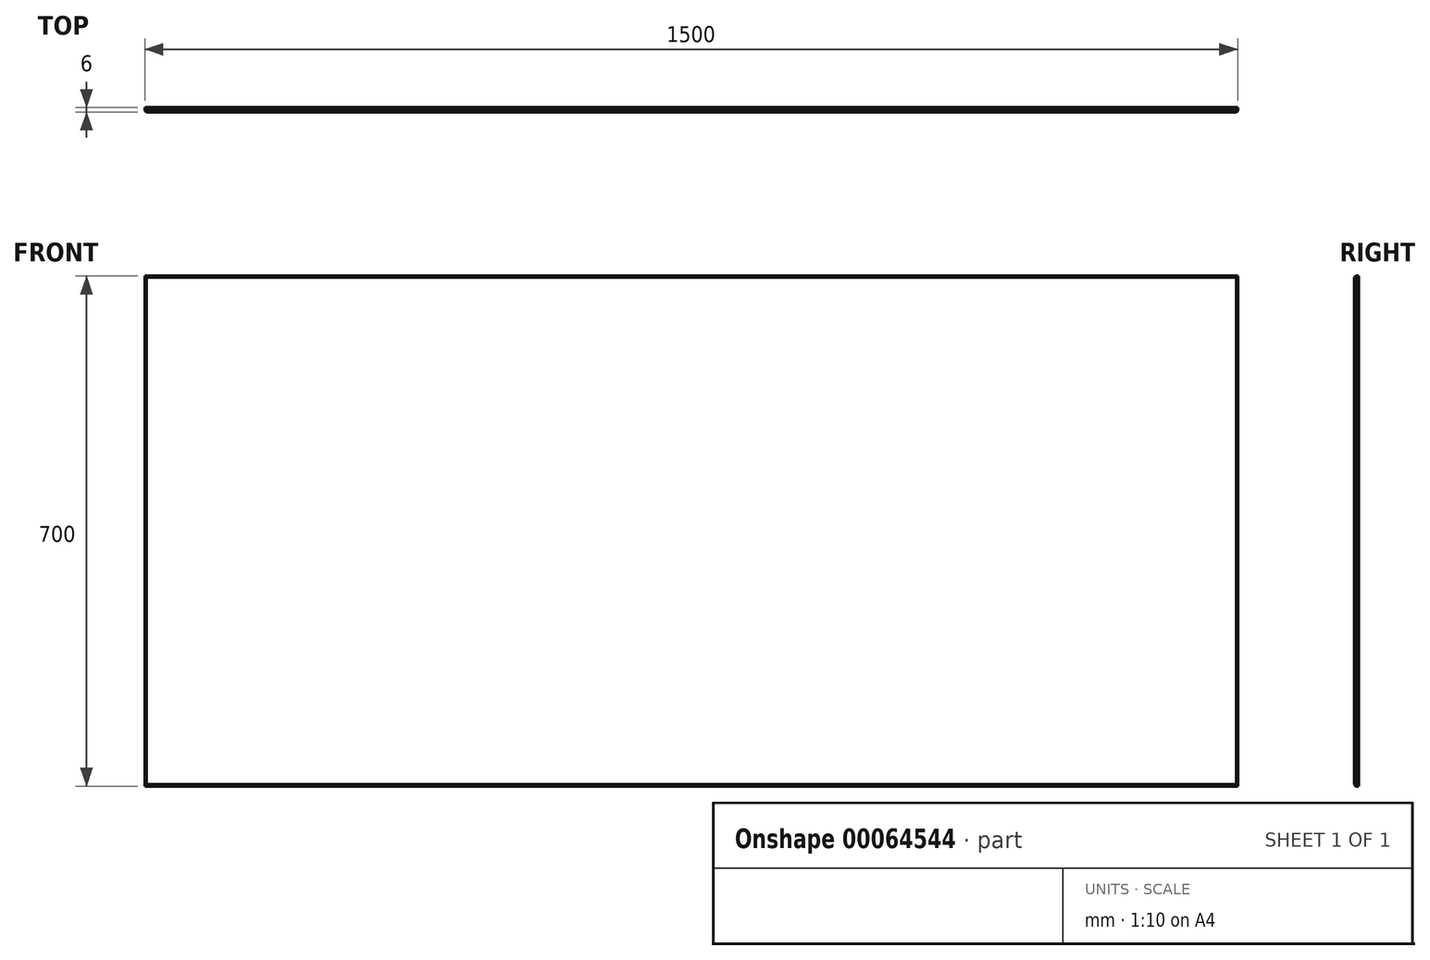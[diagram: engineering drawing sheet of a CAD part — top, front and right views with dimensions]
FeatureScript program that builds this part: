
annotation { "Feature Type Name" : "Feature", "Feature Type Description" : "" }
export const myFeature = defineFeature(function(context is Context, id is Id, definition is map)
    precondition{}
    {
        {
            var Q0;
            Q0=qCreatedBy(makeId("Front.planeOp"),FACE);
            var sketch = newSketch(context, id + "F0", { "sketchPlane" : qUnion([Q0])});
            skLineSegment(sketch, "E0.bottom", {"start": v(-741.76, 374.66) * mm, "end": v(758.24, 374.66) * mm});
            skLineSegment(sketch, "E0.top", {"start": v(-741.76, -325.34) * mm, "end": v(758.24, -325.34) * mm});
            skLineSegment(sketch, "E0.left", {"start": v(-741.76, 374.66) * mm, "end": v(-741.76, -325.34) * mm});
            skLineSegment(sketch, "E0.right", {"start": v(758.24, 374.66) * mm, "end": v(758.24, -325.34) * mm});
            skSolve(sketch);
        }
        {
            var Q0;
            Q0=makeQuery(id+"F0.imprint","IMPRINT",FACE,{"disambiguationData":[TD([[makeQuery(id+"F0.imprint","IMPRINT",EDGE,{"derivedFrom":sQuery(id+"F0.wireOp",EDGE,"E0.bottom")}),-1.0]])]});
            extrude(context, id + "F1", {"entities" : qUnion([Q0]), "depth" : 6 * mm});
        }
        {
            var Q0;
            Q0=makeQuery(id+"F1.opExtrude","CAP_FACE",FACE,{"disambiguationData":[OSD([sQuery(id+"F0.wireOp",EDGE,"E0.bottom"),sQuery(id+"F0.wireOp",EDGE,"E0.top"),sQuery(id+"F0.wireOp",EDGE,"E0.left"),sQuery(id+"F0.wireOp",EDGE,"E0.right")])],"isStart":false});
            chamfer(context, id + "F2", {"entities" : qUnion([Q0]), "width" : 2 * mm, "tangentPropagation" : true});
        }
    });
